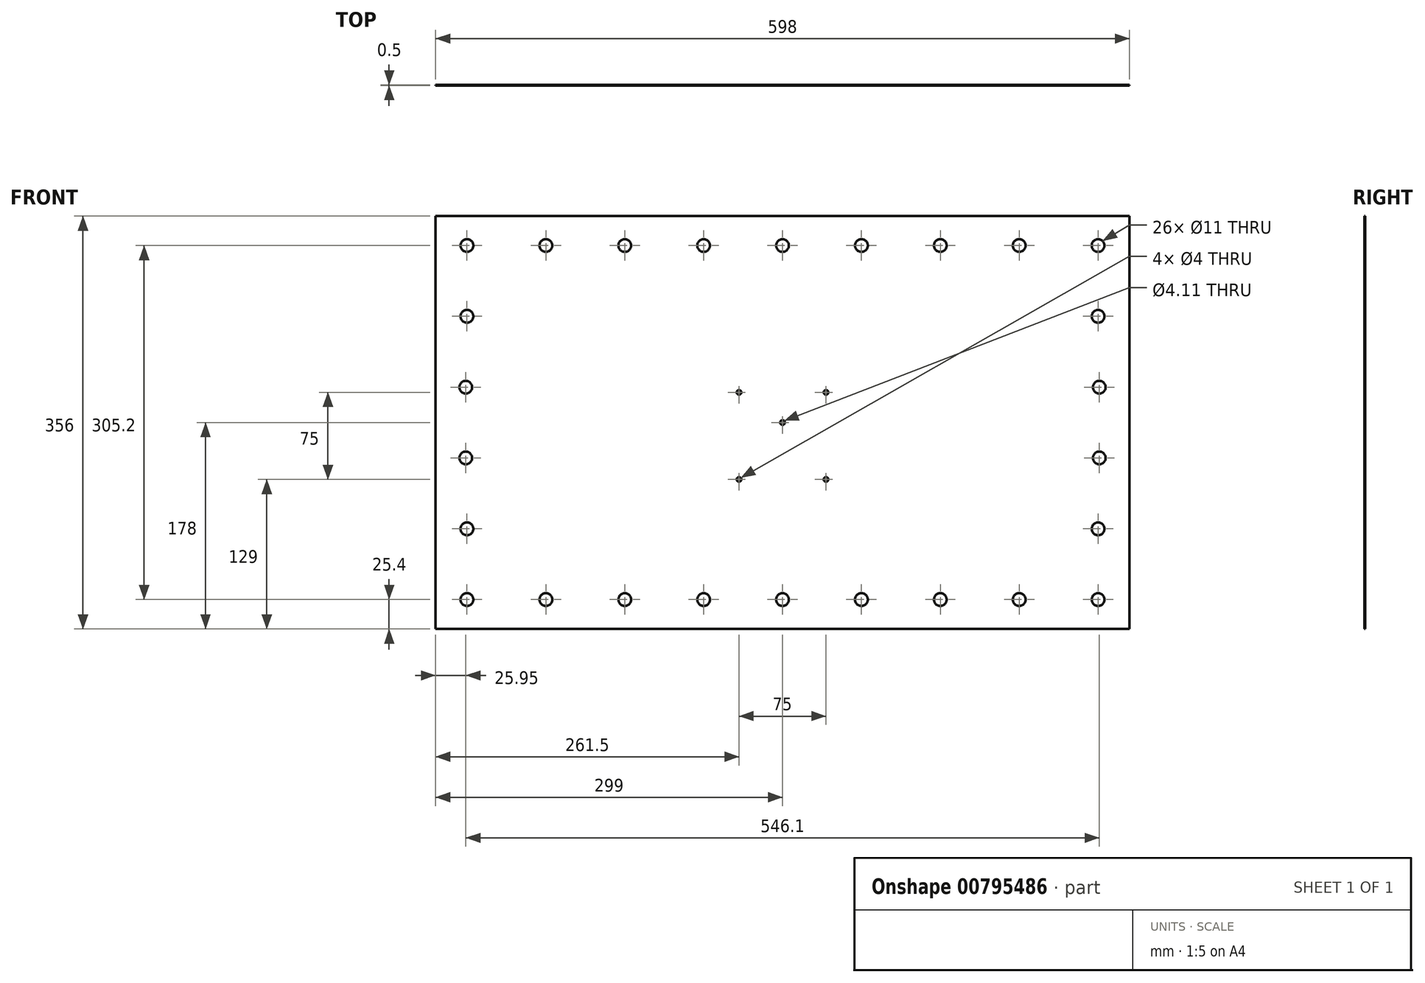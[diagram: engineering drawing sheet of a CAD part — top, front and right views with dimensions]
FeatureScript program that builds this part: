
annotation { "Feature Type Name" : "Feature", "Feature Type Description" : "" }
export const myFeature = defineFeature(function(context is Context, id is Id, definition is map)
    precondition{}
    {
        {
            var Q0;
            Q0=qCreatedBy(makeId("Front.planeOp"),FACE);
            var sketch = newSketch(context, id + "F0", { "sketchPlane" : qUnion([Q0])});
            skLineSegment(sketch, "E0.bottom", {"start": v(-299, 178) * mm, "end": v(299, 178) * mm});
            skLineSegment(sketch, "E0.top", {"start": v(-299, -178) * mm, "end": v(299, -178) * mm});
            skLineSegment(sketch, "E0.left", {"start": v(-299, 178) * mm, "end": v(-299, -178) * mm});
            skLineSegment(sketch, "E0.right", {"start": v(299, 178) * mm, "end": v(299, -178) * mm});
            skPoint(sketch, "E1", {"position": v(-37.5, 26) * mm});
            skPoint(sketch, "E2", {"position": v(37.5, 26) * mm});
            skPoint(sketch, "E3", {"position": v(37.5, -49) * mm});
            skPoint(sketch, "E4", {"position": v(-37.5, -49) * mm});
            skCircle(sketch, "E5", {"center": v(-37.5, 26) * mm, "radius": 2 * mm});
            skCircle(sketch, "E6", {"center": v(37.5, 26) * mm, "radius": 2 * mm});
            skCircle(sketch, "E7", {"center": v(37.5, -49) * mm, "radius": 2 * mm});
            skCircle(sketch, "E8", {"center": v(-37.5, -49) * mm, "radius": 2 * mm});
            skLineSegment(sketch, "E9", {"start": v(-37.5, 26) * mm, "end": v(37.5, 26) * mm, "construction": true});
            skPoint(sketch, "E10", {"position": v(0, 26) * mm});
            skPoint(sketch, "E11", {"position": v(0, 178) * mm});
            skPoint(sketch, "E12", {"position": v(0, 0) * mm});
            skCircle(sketch, "E13", {"center": v(0, 0) * mm, "radius": 2.05 * mm});
            skPoint(sketch, "E14", {"position": v(-299, 0) * mm});
            skSolve(sketch);
        }
        {
            var Q0;
            Q0 = qSketchRegion(id + "F0", true);
            extrude(context, id + "F1", {"entities" : qUnion([Q0]), "depth" : .5 * mm, "offsetDistance" : 25.4 * mm});
        }
        {
            var Q0;
            Q0=makeQuery(id+"F1.opExtrude","CAP_FACE",FACE,{"disambiguationData":[OSD([sQuery(id+"F0.wireOp",EDGE,"E0.bottom"),sQuery(id+"F0.wireOp",EDGE,"E0.top"),sQuery(id+"F0.wireOp",EDGE,"E0.left"),sQuery(id+"F0.wireOp",EDGE,"E0.right"),sQuery(id+"F0.wireOp",EDGE,"E5"),sQuery(id+"F0.wireOp",EDGE,"E6"),sQuery(id+"F0.wireOp",EDGE,"E7"),sQuery(id+"F0.wireOp",EDGE,"E8"),sQuery(id+"F0.wireOp",EDGE,"E13")])],"isStart":false});
            var sketch = newSketch(context, id + "F2", { "sketchPlane" : qUnion([Q0])});
            skCircle(sketch, "E15", {"center": v(0, 152.6) * mm, "radius": 5.5 * mm});
            skPoint(sketch, "E16", {"position": v(0, 0) * mm});
            skCircle(sketch, "E17.1.0.0", {"center": v(68, 152.6) * mm, "radius": 5.5 * mm});
            skCircle(sketch, "E17.2.0.0", {"center": v(136, 152.6) * mm, "radius": 5.5 * mm});
            skCircle(sketch, "E17.3.0.0", {"center": v(204, 152.6) * mm, "radius": 5.5 * mm});
            skCircle(sketch, "E17.4.0.0", {"center": v(272, 152.6) * mm, "radius": 5.5 * mm});
            skLineSegment(sketch, "E17.direction1", {"start": v(0, 152.6) * mm, "end": v(68, 152.6) * mm, "construction": true});
            skLineSegment(sketch, "E18", {"start": v(0, 152.6) * mm, "end": v(0, 178) * mm, "construction": true});
            skCircle(sketch, "E19.0.1.0", {"center": v(272, 91.6) * mm, "radius": 5.5 * mm});
            skCircle(sketch, "E19.0.2.0", {"center": v(273.05, 30.48) * mm, "radius": 5.5 * mm});
            skCircle(sketch, "E19.0.3.0", {"center": v(273.05, -30.48) * mm, "radius": 5.5 * mm});
            skCircle(sketch, "E19.0.4.0", {"center": v(272, -91.6) * mm, "radius": 5.5 * mm});
            skLineSegment(sketch, "E19.direction2", {"start": v(272, 152.6) * mm, "end": v(272, 91.6) * mm, "construction": true});
            skCircle(sketch, "E20.MirrorC", {"center": v(-136, 152.6) * mm, "radius": 5.5 * mm});
            skCircle(sketch, "E21.MirrorC", {"center": v(-68, 152.6) * mm, "radius": 5.5 * mm});
            skCircle(sketch, "E22.MirrorC", {"center": v(-204, 152.6) * mm, "radius": 5.5 * mm});
            skCircle(sketch, "E23.MirrorC", {"center": v(-272, 152.6) * mm, "radius": 5.5 * mm});
            skCircle(sketch, "E24.1.0", {"center": v(-272, -91.6) * mm, "radius": 5.5 * mm});
            skCircle(sketch, "E24.1.1", {"center": v(-272, -152.6) * mm, "radius": 5.5 * mm});
            skCircle(sketch, "E24.1.2", {"center": v(-204, -152.6) * mm, "radius": 5.5 * mm});
            skCircle(sketch, "E24.1.4", {"center": v(272, -152.6) * mm, "radius": 5.5 * mm});
            skCircle(sketch, "E24.1.5", {"center": v(-272, 91.6) * mm, "radius": 5.5 * mm});
            skCircle(sketch, "E24.1.6", {"center": v(-68, -152.6) * mm, "radius": 5.5 * mm});
            skCircle(sketch, "E24.1.8", {"center": v(-273.05, 30.48) * mm, "radius": 5.5 * mm});
            skCircle(sketch, "E24.1.9", {"center": v(136, -152.6) * mm, "radius": 5.5 * mm});
            skCircle(sketch, "E24.1.10", {"center": v(68, -152.6) * mm, "radius": 5.5 * mm});
            skCircle(sketch, "E24.1.11", {"center": v(0, -152.6) * mm, "radius": 5.5 * mm});
            skCircle(sketch, "E24.1.13", {"center": v(-136, -152.6) * mm, "radius": 5.5 * mm});
            skCircle(sketch, "E24.1.14", {"center": v(-273.05, -30.48) * mm, "radius": 5.5 * mm});
            skCircle(sketch, "E24.1.15", {"center": v(204, -152.6) * mm, "radius": 5.5 * mm});
            skCircle(sketch, "E24.1.16", {"center": v(-136, -152.6) * mm, "radius": 5.5 * mm});
            skCircle(sketch, "E24.1.17", {"center": v(-272, -152.6) * mm, "radius": 5.5 * mm});
            skCircle(sketch, "E24.1.18", {"center": v(136, -152.6) * mm, "radius": 5.5 * mm});
            skCircle(sketch, "E24.1.19", {"center": v(0, -152.6) * mm, "radius": 5.5 * mm});
            skCircle(sketch, "E24.1.20", {"center": v(272, -152.6) * mm, "radius": 5.5 * mm});
            skCircle(sketch, "E24.1.21", {"center": v(204, -152.6) * mm, "radius": 5.5 * mm});
            skCircle(sketch, "E24.1.22", {"center": v(-68, -152.6) * mm, "radius": 5.5 * mm});
            skCircle(sketch, "E24.1.23", {"center": v(68, -152.6) * mm, "radius": 5.5 * mm});
            skCircle(sketch, "E24.1.24", {"center": v(-204, -152.6) * mm, "radius": 5.5 * mm});
            skCircle(sketch, "E24.1.25", {"center": v(-272, -152.6) * mm, "radius": 5.5 * mm});
            skCircle(sketch, "E24.1.26", {"center": v(-136, -152.6) * mm, "radius": 5.5 * mm});
            skCircle(sketch, "E24.1.27", {"center": v(136, -152.6) * mm, "radius": 5.5 * mm});
            skCircle(sketch, "E24.1.28", {"center": v(68, -152.6) * mm, "radius": 5.5 * mm});
            skCircle(sketch, "E24.1.29", {"center": v(204, -152.6) * mm, "radius": 5.5 * mm});
            skCircle(sketch, "E24.1.30", {"center": v(-68, -152.6) * mm, "radius": 5.5 * mm});
            skCircle(sketch, "E24.1.31", {"center": v(272, -152.6) * mm, "radius": 5.5 * mm});
            skCircle(sketch, "E24.1.32", {"center": v(0, -152.6) * mm, "radius": 5.5 * mm});
            skCircle(sketch, "E24.1.33", {"center": v(-204, -152.6) * mm, "radius": 5.5 * mm});
            skCircle(sketch, "E24.1.34", {"center": v(136, -152.6) * mm, "radius": 5.5 * mm});
            skCircle(sketch, "E24.1.35", {"center": v(-68, -152.6) * mm, "radius": 5.5 * mm});
            skCircle(sketch, "E24.1.36", {"center": v(204, -152.6) * mm, "radius": 5.5 * mm});
            skCircle(sketch, "E24.1.37", {"center": v(0, -152.6) * mm, "radius": 5.5 * mm});
            skCircle(sketch, "E24.1.38", {"center": v(-136, -152.6) * mm, "radius": 5.5 * mm});
            skCircle(sketch, "E24.1.39", {"center": v(-272, -152.6) * mm, "radius": 5.5 * mm});
            skCircle(sketch, "E24.1.40", {"center": v(272, -152.6) * mm, "radius": 5.5 * mm});
            skCircle(sketch, "E24.1.41", {"center": v(-204, -152.6) * mm, "radius": 5.5 * mm});
            skCircle(sketch, "E24.1.42", {"center": v(68, -152.6) * mm, "radius": 5.5 * mm});
            skLineSegment(sketch, "E25", {"start": v(-272, 152.6) * mm, "end": v(-272, 91.6) * mm, "construction": true});
            skLineSegment(sketch, "E26", {"start": v(272, 152.6) * mm, "end": v(299, 152.6) * mm, "construction": true});
            skLineSegment(sketch, "E27", {"start": v(-272, 152.6) * mm, "end": v(-299, 152.6) * mm, "construction": true});
            skSolve(sketch);
        }
        {
            var Q0;
            Q0 = qSketchRegion(id + "F2", true);
            var Q1;
            Q1=makeQuery(id+"F1.opExtrude","CAP_FACE",FACE,{"disambiguationData":[OSD([sQuery(id+"F0.wireOp",EDGE,"E0.bottom"),sQuery(id+"F0.wireOp",EDGE,"E0.top"),sQuery(id+"F0.wireOp",EDGE,"E0.left"),sQuery(id+"F0.wireOp",EDGE,"E0.right"),sQuery(id+"F0.wireOp",EDGE,"E5"),sQuery(id+"F0.wireOp",EDGE,"E6"),sQuery(id+"F0.wireOp",EDGE,"E7"),sQuery(id+"F0.wireOp",EDGE,"E8"),sQuery(id+"F0.wireOp",EDGE,"E13")])],"isStart":true});
            extrude(context, id + "F3", {"entities" : qUnion([Q0]), "operationType" : NewBodyOperationType.REMOVE, "endBound" : BoundingType.UP_TO_NEXT, "oppositeDirection" : true, "depth" : 25 * mm, "endBoundEntityFace" : qUnion([Q1]), "offsetDistance" : 25 * mm});
        }
    });
